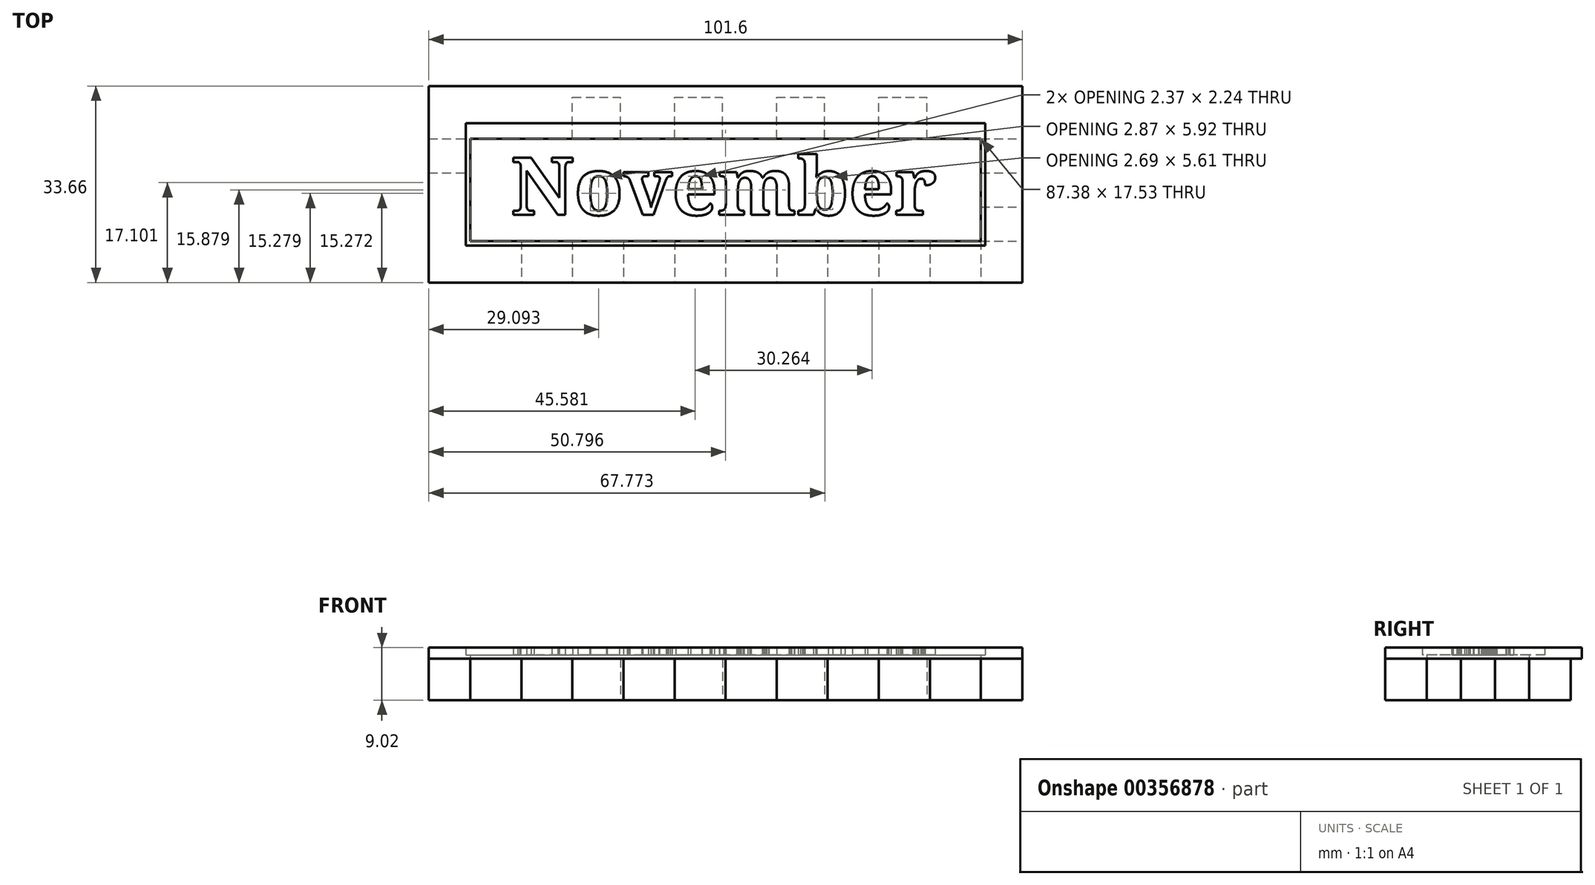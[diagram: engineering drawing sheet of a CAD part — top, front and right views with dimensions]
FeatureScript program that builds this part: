
annotation { "Feature Type Name" : "Feature", "Feature Type Description" : "" }
export const myFeature = defineFeature(function(context is Context, id is Id, definition is map)
    precondition{}
    {
        {
            var Q0;
            Q0=qCreatedBy(makeId("Top.planeOp"),FACE);
            var sketch = newSketch(context, id + "F0", { "sketchPlane" : qUnion([Q0])});
            skLineSegment(sketch, "E0.bottom", {"start": v(-52.12, 11.37) * mm, "end": v(49.48, 11.37) * mm});
            skLineSegment(sketch, "E0.top", {"start": v(-52.12, -20.38) * mm, "end": v(49.48, -20.38) * mm});
            skLineSegment(sketch, "E0.left", {"start": v(-52.12, 11.37) * mm, "end": v(-52.12, -20.38) * mm});
            skLineSegment(sketch, "E0.right", {"start": v(49.48, 11.37) * mm, "end": v(49.48, -20.38) * mm});
            skLineSegment(sketch, "E1.bottom", {"start": v(-52.12, 11.37) * mm, "end": v(-45.01, 11.37) * mm});
            skLineSegment(sketch, "E1.top", {"start": v(-52.12, 4.26) * mm, "end": v(-45.01, 4.26) * mm});
            skLineSegment(sketch, "E1.left", {"start": v(-52.12, 11.37) * mm, "end": v(-52.12, 4.26) * mm});
            skLineSegment(sketch, "E1.right", {"start": v(-45.01, 11.37) * mm, "end": v(-45.01, 4.26) * mm});
            skLineSegment(sketch, "E2.bottom", {"start": v(-45.01, 11.37) * mm, "end": v(-36.78, 11.37) * mm});
            skLineSegment(sketch, "E2.top", {"start": v(-45.01, 4.26) * mm, "end": v(-36.78, 4.26) * mm});
            skLineSegment(sketch, "E2.right", {"start": v(-36.78, 11.37) * mm, "end": v(-36.78, 4.26) * mm});
            skLineSegment(sketch, "E3.bottom", {"start": v(-36.78, 4.26) * mm, "end": v(-27.54, 4.26) * mm});
            skLineSegment(sketch, "E3.top", {"start": v(-36.78, 11.37) * mm, "end": v(-27.54, 11.37) * mm});
            skLineSegment(sketch, "E3.left", {"start": v(-36.78, 4.26) * mm, "end": v(-36.78, 11.37) * mm});
            skLineSegment(sketch, "E3.right", {"start": v(-27.54, 4.26) * mm, "end": v(-27.54, 11.37) * mm});
            skLineSegment(sketch, "E4.bottom", {"start": v(-27.54, 4.26) * mm, "end": v(-19.3, 4.26) * mm});
            skLineSegment(sketch, "E4.top", {"start": v(-27.54, 11.37) * mm, "end": v(-19.3, 11.37) * mm});
            skLineSegment(sketch, "E4.right", {"start": v(-19.3, 4.26) * mm, "end": v(-19.3, 11.37) * mm});
            skLineSegment(sketch, "E5.bottom", {"start": v(-19.3, 4.26) * mm, "end": v(-10.06, 4.26) * mm});
            skLineSegment(sketch, "E5.top", {"start": v(-19.3, 11.37) * mm, "end": v(-10.06, 11.37) * mm});
            skLineSegment(sketch, "E5.right", {"start": v(-10.06, 4.26) * mm, "end": v(-10.06, 11.37) * mm});
            skLineSegment(sketch, "E6.bottom", {"start": v(-10.06, 4.26) * mm, "end": v(-10.06, 4.26) * mm});
            skLineSegment(sketch, "E6.top", {"start": v(-10.06, 11.37) * mm, "end": v(-10.06, 11.37) * mm});
            skLineSegment(sketch, "E7.bottom", {"start": v(-10.06, 4.26) * mm, "end": v(-1.83, 4.26) * mm});
            skLineSegment(sketch, "E7.top", {"start": v(-10.06, 11.37) * mm, "end": v(-1.83, 11.37) * mm});
            skLineSegment(sketch, "E7.right", {"start": v(-1.83, 4.26) * mm, "end": v(-1.83, 11.37) * mm});
            skLineSegment(sketch, "E8.bottom", {"start": v(-1.83, 4.26) * mm, "end": v(7.41, 4.26) * mm});
            skLineSegment(sketch, "E8.top", {"start": v(-1.83, 11.37) * mm, "end": v(7.41, 11.37) * mm});
            skLineSegment(sketch, "E8.right", {"start": v(7.41, 4.26) * mm, "end": v(7.41, 11.37) * mm});
            skLineSegment(sketch, "E9.bottom", {"start": v(7.41, 4.26) * mm, "end": v(15.64, 4.26) * mm});
            skLineSegment(sketch, "E9.top", {"start": v(7.41, 11.37) * mm, "end": v(15.64, 11.37) * mm});
            skLineSegment(sketch, "E9.right", {"start": v(15.64, 4.26) * mm, "end": v(15.64, 11.37) * mm});
            skLineSegment(sketch, "E10.bottom", {"start": v(15.64, 4.26) * mm, "end": v(24.89, 4.26) * mm});
            skLineSegment(sketch, "E10.top", {"start": v(15.64, 11.37) * mm, "end": v(24.89, 11.37) * mm});
            skLineSegment(sketch, "E10.right", {"start": v(24.89, 4.26) * mm, "end": v(24.89, 11.37) * mm});
            skLineSegment(sketch, "E11.bottom", {"start": v(24.89, 4.26) * mm, "end": v(24.89, 4.26) * mm});
            skLineSegment(sketch, "E11.top", {"start": v(24.89, 11.37) * mm, "end": v(24.89, 11.37) * mm});
            skLineSegment(sketch, "E12.bottom", {"start": v(24.89, 4.26) * mm, "end": v(33.12, 4.26) * mm});
            skLineSegment(sketch, "E12.top", {"start": v(24.89, 11.37) * mm, "end": v(33.12, 11.37) * mm});
            skLineSegment(sketch, "E12.right", {"start": v(33.12, 4.26) * mm, "end": v(33.12, 11.37) * mm});
            skLineSegment(sketch, "E13.bottom", {"start": v(33.12, 4.26) * mm, "end": v(42.36, 4.26) * mm});
            skLineSegment(sketch, "E13.top", {"start": v(33.12, 11.37) * mm, "end": v(42.36, 11.37) * mm});
            skLineSegment(sketch, "E13.right", {"start": v(42.36, 4.26) * mm, "end": v(42.36, 11.37) * mm});
            skLineSegment(sketch, "E14.bottom", {"start": v(42.36, 4.26) * mm, "end": v(49.48, 4.26) * mm});
            skLineSegment(sketch, "E14.top", {"start": v(42.36, 11.37) * mm, "end": v(49.48, 11.37) * mm});
            skLineSegment(sketch, "E14.right", {"start": v(49.48, 4.26) * mm, "end": v(49.48, 11.37) * mm});
            skLineSegment(sketch, "E15.bottom", {"start": v(-52.12, -20.38) * mm, "end": v(-45.01, -20.38) * mm});
            skLineSegment(sketch, "E15.top", {"start": v(-52.12, -13.26) * mm, "end": v(-45.01, -13.26) * mm});
            skLineSegment(sketch, "E15.left", {"start": v(-52.12, -20.38) * mm, "end": v(-52.12, -13.26) * mm});
            skLineSegment(sketch, "E15.right", {"start": v(-45.01, -20.38) * mm, "end": v(-45.01, -13.26) * mm});
            skLineSegment(sketch, "E16.bottom", {"start": v(-45.01, -13.26) * mm, "end": v(-45.01, -13.26) * mm});
            skLineSegment(sketch, "E16.top", {"start": v(-45.01, -20.38) * mm, "end": v(-45.01, -20.38) * mm});
            skLineSegment(sketch, "E16.left", {"start": v(-45.01, -13.26) * mm, "end": v(-45.01, -20.38) * mm});
            skLineSegment(sketch, "E16.right", {"start": v(-45.01, -13.26) * mm, "end": v(-45.01, -20.38) * mm});
            skLineSegment(sketch, "E17.bottom", {"start": v(-45.01, -13.26) * mm, "end": v(-36.27, -13.26) * mm});
            skLineSegment(sketch, "E17.top", {"start": v(-45.01, -20.38) * mm, "end": v(-36.27, -20.38) * mm});
            skLineSegment(sketch, "E17.right", {"start": v(-36.27, -13.26) * mm, "end": v(-36.27, -20.38) * mm});
            skLineSegment(sketch, "E18.bottom", {"start": v(-36.27, -13.26) * mm, "end": v(-36.27, -13.26) * mm});
            skLineSegment(sketch, "E18.top", {"start": v(-36.27, -20.38) * mm, "end": v(-36.27, -20.38) * mm});
            skLineSegment(sketch, "E19.bottom", {"start": v(-36.27, -13.26) * mm, "end": v(-27.54, -13.26) * mm});
            skLineSegment(sketch, "E19.top", {"start": v(-36.27, -20.38) * mm, "end": v(-27.54, -20.38) * mm});
            skLineSegment(sketch, "E19.right", {"start": v(-27.54, -13.26) * mm, "end": v(-27.54, -20.38) * mm});
            skLineSegment(sketch, "E20.bottom", {"start": v(-27.54, -13.26) * mm, "end": v(-18.8, -13.26) * mm});
            skLineSegment(sketch, "E20.top", {"start": v(-27.54, -20.38) * mm, "end": v(-18.8, -20.38) * mm});
            skLineSegment(sketch, "E20.right", {"start": v(-18.8, -13.26) * mm, "end": v(-18.8, -20.38) * mm});
            skLineSegment(sketch, "E21.bottom", {"start": v(-18.8, -13.26) * mm, "end": v(-10.06, -13.26) * mm});
            skLineSegment(sketch, "E21.top", {"start": v(-18.8, -20.38) * mm, "end": v(-10.06, -20.38) * mm});
            skLineSegment(sketch, "E21.right", {"start": v(-10.06, -13.26) * mm, "end": v(-10.06, -20.38) * mm});
            skLineSegment(sketch, "E22.bottom", {"start": v(-10.06, -13.26) * mm, "end": v(-1.32, -13.26) * mm});
            skLineSegment(sketch, "E22.top", {"start": v(-10.06, -20.38) * mm, "end": v(-1.32, -20.38) * mm});
            skLineSegment(sketch, "E22.right", {"start": v(-1.32, -13.26) * mm, "end": v(-1.32, -20.38) * mm});
            skLineSegment(sketch, "E23.bottom", {"start": v(-1.32, -13.26) * mm, "end": v(7.41, -13.26) * mm});
            skLineSegment(sketch, "E23.top", {"start": v(-1.32, -20.38) * mm, "end": v(7.41, -20.38) * mm});
            skLineSegment(sketch, "E23.right", {"start": v(7.41, -13.26) * mm, "end": v(7.41, -20.38) * mm});
            skLineSegment(sketch, "E24.bottom", {"start": v(7.41, -13.26) * mm, "end": v(16.15, -13.26) * mm});
            skLineSegment(sketch, "E24.top", {"start": v(7.41, -20.38) * mm, "end": v(16.15, -20.38) * mm});
            skLineSegment(sketch, "E24.right", {"start": v(16.15, -13.26) * mm, "end": v(16.15, -20.38) * mm});
            skLineSegment(sketch, "E25.bottom", {"start": v(16.15, -13.26) * mm, "end": v(24.89, -13.26) * mm});
            skLineSegment(sketch, "E25.top", {"start": v(16.15, -20.38) * mm, "end": v(24.89, -20.38) * mm});
            skLineSegment(sketch, "E25.right", {"start": v(24.89, -13.26) * mm, "end": v(24.89, -20.38) * mm});
            skLineSegment(sketch, "E26.bottom", {"start": v(24.89, -13.26) * mm, "end": v(33.63, -13.26) * mm});
            skLineSegment(sketch, "E26.top", {"start": v(24.89, -20.38) * mm, "end": v(33.63, -20.38) * mm});
            skLineSegment(sketch, "E26.right", {"start": v(33.63, -13.26) * mm, "end": v(33.63, -20.38) * mm});
            skLineSegment(sketch, "E27.bottom", {"start": v(33.63, -13.26) * mm, "end": v(42.36, -13.26) * mm});
            skLineSegment(sketch, "E27.top", {"start": v(33.63, -20.38) * mm, "end": v(42.36, -20.38) * mm});
            skLineSegment(sketch, "E27.right", {"start": v(42.36, -13.26) * mm, "end": v(42.36, -20.38) * mm});
            skLineSegment(sketch, "E28.bottom", {"start": v(42.36, -13.26) * mm, "end": v(49.48, -13.26) * mm});
            skLineSegment(sketch, "E28.top", {"start": v(42.36, -20.38) * mm, "end": v(49.48, -20.38) * mm});
            skLineSegment(sketch, "E28.right", {"start": v(49.48, -13.26) * mm, "end": v(49.48, -20.38) * mm});
            skLineSegment(sketch, "E29.top", {"start": v(-52.12, -1.58) * mm, "end": v(-45.01, -1.58) * mm});
            skLineSegment(sketch, "E29.left", {"start": v(-52.12, 4.26) * mm, "end": v(-52.12, -1.58) * mm});
            skLineSegment(sketch, "E29.right", {"start": v(-45.01, 4.26) * mm, "end": v(-45.01, -1.58) * mm});
            skLineSegment(sketch, "E30.top", {"start": v(-52.12, -7.42) * mm, "end": v(-45.01, -7.42) * mm});
            skLineSegment(sketch, "E30.left", {"start": v(-52.12, -1.58) * mm, "end": v(-52.12, -7.42) * mm});
            skLineSegment(sketch, "E30.right", {"start": v(-45.01, -1.58) * mm, "end": v(-45.01, -7.42) * mm});
            skLineSegment(sketch, "E31.bottom", {"start": v(-45.01, -7.42) * mm, "end": v(-52.12, -7.42) * mm});
            skLineSegment(sketch, "E31.top", {"start": v(-45.01, -13.26) * mm, "end": v(-52.12, -13.26) * mm});
            skLineSegment(sketch, "E31.left", {"start": v(-45.01, -7.42) * mm, "end": v(-45.01, -13.26) * mm});
            skLineSegment(sketch, "E31.right", {"start": v(-52.12, -7.42) * mm, "end": v(-52.12, -13.26) * mm});
            skLineSegment(sketch, "E32.top", {"start": v(42.36, -1.58) * mm, "end": v(49.48, -1.58) * mm});
            skLineSegment(sketch, "E32.left", {"start": v(42.36, 4.26) * mm, "end": v(42.36, -1.58) * mm});
            skLineSegment(sketch, "E32.right", {"start": v(49.48, 4.26) * mm, "end": v(49.48, -1.58) * mm});
            skLineSegment(sketch, "E33.top", {"start": v(42.36, -7.42) * mm, "end": v(49.48, -7.42) * mm});
            skLineSegment(sketch, "E33.left", {"start": v(42.36, -1.58) * mm, "end": v(42.36, -7.42) * mm});
            skLineSegment(sketch, "E33.right", {"start": v(49.48, -1.58) * mm, "end": v(49.48, -7.42) * mm});
            skLineSegment(sketch, "E34.left", {"start": v(42.36, -7.42) * mm, "end": v(42.36, -13.26) * mm});
            skLineSegment(sketch, "E34.right", {"start": v(49.48, -7.42) * mm, "end": v(49.48, -13.26) * mm});
            skSolve(sketch);
        }
        {
            var Q0;
            Q0=makeQuery(id+"F0.imprint","IMPRINT",FACE,{"disambiguationData":[TD([[makeQuery(id+"F0.imprint","IMPRINT",EDGE,{"derivedFrom":sQuery(id+"F0.wireOp",EDGE,"E2.top")}),-1.0]])]});
            var Q1;
            Q1=makeQuery(id+"F0.imprint","IMPRINT",FACE,{"disambiguationData":[TD([[makeQuery(id+"F0.imprint","IMPRINT",EDGE,{"derivedFrom":sQuery(id+"F0.wireOp",EDGE,"E2.bottom")}),-1.0]])]});
            var Q2;
            Q2=makeQuery(id+"F0.imprint","IMPRINT",FACE,{"disambiguationData":[TD([[makeQuery(id+"F0.imprint","IMPRINT",EDGE,{"derivedFrom":sQuery(id+"F0.wireOp",EDGE,"E4.bottom")}),1.0]])]});
            var Q3;
            Q3=makeQuery(id+"F0.imprint","IMPRINT",FACE,{"disambiguationData":[TD([[makeQuery(id+"F0.imprint","IMPRINT",EDGE,{"derivedFrom":sQuery(id+"F0.wireOp",EDGE,"E7.bottom")}),1.0]])]});
            var Q4;
            Q4=makeQuery(id+"F0.imprint","IMPRINT",FACE,{"disambiguationData":[TD([[makeQuery(id+"F0.imprint","IMPRINT",EDGE,{"derivedFrom":sQuery(id+"F0.wireOp",EDGE,"E9.bottom")}),1.0]])]});
            var Q5;
            Q5=makeQuery(id+"F0.imprint","IMPRINT",FACE,{"disambiguationData":[TD([[makeQuery(id+"F0.imprint","IMPRINT",EDGE,{"derivedFrom":sQuery(id+"F0.wireOp",EDGE,"E12.bottom")}),1.0]])]});
            var Q6;
            Q6=makeQuery(id+"F0.imprint","IMPRINT",FACE,{"disambiguationData":[TD([[makeQuery(id+"F0.imprint","IMPRINT",EDGE,{"derivedFrom":sQuery(id+"F0.wireOp",EDGE,"E14.bottom")}),-1.0]])]});
            var Q7;
            Q7=makeQuery(id+"F0.imprint","IMPRINT",FACE,{"disambiguationData":[TD([[makeQuery(id+"F0.imprint","IMPRINT",EDGE,{"derivedFrom":sQuery(id+"F0.wireOp",EDGE,"E33.top")}),-1.0]])]});
            var Q8;
            Q8=makeQuery(id+"F0.imprint","IMPRINT",FACE,{"disambiguationData":[TD([[makeQuery(id+"F0.imprint","IMPRINT",EDGE,{"derivedFrom":sQuery(id+"F0.wireOp",EDGE,"E27.bottom")}),-1.0]])]});
            var Q9;
            Q9=makeQuery(id+"F0.imprint","IMPRINT",FACE,{"disambiguationData":[TD([[makeQuery(id+"F0.imprint","IMPRINT",EDGE,{"derivedFrom":sQuery(id+"F0.wireOp",EDGE,"E25.bottom")}),-1.0]])]});
            var Q10;
            Q10=makeQuery(id+"F0.imprint","IMPRINT",FACE,{"disambiguationData":[TD([[makeQuery(id+"F0.imprint","IMPRINT",EDGE,{"derivedFrom":sQuery(id+"F0.wireOp",EDGE,"E23.bottom")}),-1.0]])]});
            var Q11;
            Q11=makeQuery(id+"F0.imprint","IMPRINT",FACE,{"disambiguationData":[TD([[makeQuery(id+"F0.imprint","IMPRINT",EDGE,{"derivedFrom":sQuery(id+"F0.wireOp",EDGE,"E21.bottom")}),-1.0]])]});
            var Q12;
            Q12=makeQuery(id+"F0.imprint","IMPRINT",FACE,{"disambiguationData":[TD([[makeQuery(id+"F0.imprint","IMPRINT",EDGE,{"derivedFrom":sQuery(id+"F0.wireOp",EDGE,"E19.bottom")}),-1.0]])]});
            var Q13;
            Q13=makeQuery(id+"F0.imprint","IMPRINT",FACE,{"disambiguationData":[TD([[makeQuery(id+"F0.imprint","IMPRINT",EDGE,{"derivedFrom":sQuery(id+"F0.wireOp",EDGE,"E31.bottom")}),1.0]])]});
            var Q14;
            Q14=makeQuery(id+"F0.imprint","IMPRINT",FACE,{"disambiguationData":[TD([[makeQuery(id+"F0.imprint","IMPRINT",EDGE,{"derivedFrom":sQuery(id+"F0.wireOp",EDGE,"E1.top")}),-1.0]])]});
            extrude(context, id + "F1", {"entities" : qUnion([Q0, Q1, Q2, Q3, Q4, Q5, Q6, Q7, Q8, Q9, Q10, Q11, Q12, Q13, Q14]), "depth" : 7.11 * mm});
        }
        {
            var Q0;
            Q0=makeQuery(id+"F1.opExtrude","CAP_FACE",FACE,{"disambiguationData":[OSD([sQuery(id+"F0.wireOp",EDGE,"E2.bottom"),sQuery(id+"F0.wireOp",EDGE,"E1.right"),sQuery(id+"F0.wireOp",EDGE,"E3.bottom"),sQuery(id+"F0.wireOp",EDGE,"E3.left"),sQuery(id+"F0.wireOp",EDGE,"E4.top"),sQuery(id+"F0.wireOp",EDGE,"E3.right"),sQuery(id+"F0.wireOp",EDGE,"E5.bottom"),sQuery(id+"F0.wireOp",EDGE,"E4.right"),sQuery(id+"F0.wireOp",EDGE,"E6.top"),sQuery(id+"F0.wireOp",EDGE,"E5.right"),sQuery(id+"F0.wireOp",EDGE,"E7.bottom"),sQuery(id+"F0.wireOp",EDGE,"E5.right"),sQuery(id+"F0.wireOp",EDGE,"E8.top"),sQuery(id+"F0.wireOp",EDGE,"E7.right"),sQuery(id+"F0.wireOp",EDGE,"E9.bottom"),sQuery(id+"F0.wireOp",EDGE,"E8.right"),sQuery(id+"F0.wireOp",EDGE,"E10.top"),sQuery(id+"F0.wireOp",EDGE,"E9.right"),sQuery(id+"F0.wireOp",EDGE,"E11.bottom"),sQuery(id+"F0.wireOp",EDGE,"E10.right"),sQuery(id+"F0.wireOp",EDGE,"E12.top"),sQuery(id+"F0.wireOp",EDGE,"E10.right"),sQuery(id+"F0.wireOp",EDGE,"E13.bottom"),sQuery(id+"F0.wireOp",EDGE,"E12.right"),sQuery(id+"F0.wireOp",EDGE,"E16.bottom"),sQuery(id+"F0.wireOp",EDGE,"E17.top"),sQuery(id+"F0.wireOp",EDGE,"E16.left"),sQuery(id+"F0.wireOp",EDGE,"E18.bottom"),sQuery(id+"F0.wireOp",EDGE,"E17.right"),sQuery(id+"F0.wireOp",EDGE,"E19.top"),sQuery(id+"F0.wireOp",EDGE,"E17.right"),sQuery(id+"F0.wireOp",EDGE,"E20.bottom"),sQuery(id+"F0.wireOp",EDGE,"E19.right"),sQuery(id+"F0.wireOp",EDGE,"E21.top"),sQuery(id+"F0.wireOp",EDGE,"E20.right"),sQuery(id+"F0.wireOp",EDGE,"E22.bottom"),sQuery(id+"F0.wireOp",EDGE,"E21.right"),sQuery(id+"F0.wireOp",EDGE,"E23.top"),sQuery(id+"F0.wireOp",EDGE,"E22.right"),sQuery(id+"F0.wireOp",EDGE,"E24.bottom"),sQuery(id+"F0.wireOp",EDGE,"E23.right"),sQuery(id+"F0.wireOp",EDGE,"E25.top"),sQuery(id+"F0.wireOp",EDGE,"E24.right"),sQuery(id+"F0.wireOp",EDGE,"E26.bottom"),sQuery(id+"F0.wireOp",EDGE,"E25.right"),sQuery(id+"F0.wireOp",EDGE,"E27.top"),sQuery(id+"F0.wireOp",EDGE,"E26.right"),sQuery(id+"F0.wireOp",EDGE,"E27.right"),sQuery(id+"F0.wireOp",EDGE,"E1.top"),sQuery(id+"F0.wireOp",EDGE,"E29.left"),sQuery(id+"F0.wireOp",EDGE,"E29.top"),sQuery(id+"F0.wireOp",EDGE,"E30.right"),sQuery(id+"F0.wireOp",EDGE,"E31.bottom"),sQuery(id+"F0.wireOp",EDGE,"E31.top"),sQuery(id+"F0.wireOp",EDGE,"E31.right"),sQuery(id+"F0.wireOp",EDGE,"E14.bottom"),sQuery(id+"F0.wireOp",EDGE,"E32.right"),sQuery(id+"F0.wireOp",EDGE,"E32.top"),sQuery(id+"F0.wireOp",EDGE,"E33.left"),sQuery(id+"F0.wireOp",EDGE,"E33.top"),sQuery(id+"F0.wireOp",EDGE,"E28.bottom"),sQuery(id+"F0.wireOp",EDGE,"E34.right")])],"isStart":false});
            var sketch = newSketch(context, id + "F2", { "sketchPlane" : qUnion([Q0])});
            skLineSegment(sketch, "E35.bottom", {"start": v(-52.12, -20.38) * mm, "end": v(-45.01, -20.38) * mm});
            skLineSegment(sketch, "E35.top", {"start": v(-52.12, 13.28) * mm, "end": v(-45.01, 13.28) * mm});
            skLineSegment(sketch, "E35.left", {"start": v(-52.12, -20.38) * mm, "end": v(-52.12, 13.28) * mm});
            skLineSegment(sketch, "E35.right", {"start": v(-45.01, -20.38) * mm, "end": v(-45.01, 13.28) * mm});
            skLineSegment(sketch, "E36.bottom", {"start": v(-52.12, -20.38) * mm, "end": v(49.48, -20.38) * mm});
            skLineSegment(sketch, "E36.top", {"start": v(-52.12, -13.26) * mm, "end": v(49.48, -13.26) * mm});
            skLineSegment(sketch, "E36.left", {"start": v(-52.12, -20.38) * mm, "end": v(-52.12, -13.26) * mm});
            skLineSegment(sketch, "E36.right", {"start": v(49.48, -20.38) * mm, "end": v(49.48, -13.26) * mm});
            skPoint(sketch, "E37.oppositeSnap0", {"position": v(42.36, -4.5) * mm});
            skLineSegment(sketch, "E37.bottom", {"start": v(49.48, -20.38) * mm, "end": v(42.36, -20.38) * mm});
            skLineSegment(sketch, "E37.top", {"start": v(49.48, 13.28) * mm, "end": v(42.36, 13.28) * mm});
            skLineSegment(sketch, "E37.left", {"start": v(49.48, -20.38) * mm, "end": v(49.48, 13.28) * mm});
            skLineSegment(sketch, "E37.right", {"start": v(42.36, -20.38) * mm, "end": v(42.36, 13.28) * mm});
            skLineSegment(sketch, "E38.bottom", {"start": v(-52.12, 13.28) * mm, "end": v(49.48, 13.28) * mm});
            skLineSegment(sketch, "E38.top", {"start": v(-52.12, 4.26) * mm, "end": v(49.48, 4.26) * mm});
            skLineSegment(sketch, "E38.left", {"start": v(-52.12, 13.28) * mm, "end": v(-52.12, 4.26) * mm});
            skLineSegment(sketch, "E38.right", {"start": v(49.48, 13.28) * mm, "end": v(49.48, 4.26) * mm});
            skSolve(sketch);
        }
        {
            var Q0;
            Q0=qSketchRegion(id+"F2",true);
            var Q1;
            {var subQ5=sQuery(id+"F2.wireOp",EDGE,"E36.top");var subQ10=sQuery(id+"F2.wireOp",EDGE,"E35.right");var subQ12=makeQuery(id+"F2.imprint","INTERSECT",VERTEX,{"derivedFrom":[makeQuery(id+"F1.opExtrude","CAP_EDGE",EDGE,{"disambiguationData":[OSD([sQuery(id+"F0.wireOp",EDGE,"E31.bottom")])],"isStart":false}),subQ10]});var subQ24=makeQuery(id+"F2.imprint","INTERSECT",VERTEX,{"derivedFrom":[subQ10,subQ5]});Q1=makeQuery(id+"F2.imprint","IMPRINT",FACE,{"disambiguationData":[TD([[makeQuery(id+"F2.imprint","IMPRINT",EDGE,{"disambiguationData":[TD([[subQ12,1.0],[subQ24,-1.0]])],"derivedFrom":subQ10}),-1.0]])]});}
            extrude(context, id + "F3", {"entities" : qUnion([Q0, Q1]), "depth" : 0.64 * mm});
        }
        {
            var Q0;
            Q0=makeQuery(id+"F3.opExtrude","CAP_FACE",FACE,{"disambiguationData":[OSD([sQuery(id+"F2.wireOp",EDGE,"E35.left"),sQuery(id+"F2.wireOp",EDGE,"E36.bottom"),sQuery(id+"F2.wireOp",EDGE,"E36.left"),sQuery(id+"F2.wireOp",EDGE,"E37.bottom"),sQuery(id+"F2.wireOp",EDGE,"E37.left"),sQuery(id+"F2.wireOp",EDGE,"E38.bottom"),sQuery(id+"F2.wireOp",EDGE,"E38.left"),sQuery(id+"F2.wireOp",EDGE,"E38.right")])],"isStart":false});
            var sketch = newSketch(context, id + "F4", { "sketchPlane" : qUnion([Q0])});
            skLineSegment(sketch, "E39.bottom", {"start": v(-52.12, 13.28) * mm, "end": v(49.48, 13.28) * mm});
            skLineSegment(sketch, "E39.top", {"start": v(-52.12, 6.93) * mm, "end": v(49.48, 6.93) * mm});
            skLineSegment(sketch, "E39.left", {"start": v(-52.12, 13.28) * mm, "end": v(-52.12, 6.93) * mm});
            skLineSegment(sketch, "E39.right", {"start": v(49.48, 13.28) * mm, "end": v(49.48, 6.93) * mm});
            skLineSegment(sketch, "E40.bottom", {"start": v(-52.12, 13.28) * mm, "end": v(-45.77, 13.28) * mm});
            skLineSegment(sketch, "E40.top", {"start": v(-52.12, -20.38) * mm, "end": v(-45.77, -20.38) * mm});
            skLineSegment(sketch, "E40.left", {"start": v(-52.12, 13.28) * mm, "end": v(-52.12, -20.38) * mm});
            skLineSegment(sketch, "E40.right", {"start": v(-45.77, 13.28) * mm, "end": v(-45.77, -20.38) * mm});
            skLineSegment(sketch, "E41.bottom", {"start": v(-52.12, -14.03) * mm, "end": v(49.48, -14.03) * mm});
            skLineSegment(sketch, "E41.top", {"start": v(-52.12, -20.38) * mm, "end": v(49.48, -20.38) * mm});
            skLineSegment(sketch, "E41.left", {"start": v(-52.12, -14.03) * mm, "end": v(-52.12, -20.38) * mm});
            skLineSegment(sketch, "E41.right", {"start": v(49.48, -14.03) * mm, "end": v(49.48, -20.38) * mm});
            skLineSegment(sketch, "E42.bottom", {"start": v(49.48, -20.38) * mm, "end": v(43.13, -20.38) * mm});
            skLineSegment(sketch, "E42.top", {"start": v(49.48, 13.28) * mm, "end": v(43.13, 13.28) * mm});
            skLineSegment(sketch, "E42.left", {"start": v(49.48, -20.38) * mm, "end": v(49.48, 13.28) * mm});
            skLineSegment(sketch, "E42.right", {"start": v(43.13, -20.38) * mm, "end": v(43.13, 13.28) * mm});
            skSolve(sketch);
        }
        {
            var Q0;
            Q0=qSketchRegion(id+"F4",true);
            extrude(context, id + "F5", {"entities" : qUnion([Q0]), "operationType" : NewBodyOperationType.ADD, "depth" : 1.27 * mm});
        }
        {
            var Q0;
            Q0=makeQuery(id+"F3.opExtrude","CAP_FACE",FACE,{"disambiguationData":[OSD([sQuery(id+"F2.wireOp",EDGE,"E35.left"),sQuery(id+"F2.wireOp",EDGE,"E36.bottom"),sQuery(id+"F2.wireOp",EDGE,"E36.left"),sQuery(id+"F2.wireOp",EDGE,"E37.bottom"),sQuery(id+"F2.wireOp",EDGE,"E37.left"),sQuery(id+"F2.wireOp",EDGE,"E38.bottom"),sQuery(id+"F2.wireOp",EDGE,"E38.left"),sQuery(id+"F2.wireOp",EDGE,"E38.right")])],"isStart":false});
            var sketch = newSketch(context, id + "F6", { "sketchPlane" : qUnion([Q0])});
            skText(sketch, "E43", { "text": "November", "fontName": "NotoSerif-Bold.ttf"});
            const initialGuessF6  = {"E43": [-0.03805, -0.0088, 1, 0, 0.00988]};
            skSetInitialGuess(sketch, initialGuessF6);
            skSolve(sketch);
        }
        {
            var Q0;
            Q0 = qSketchRegion(id + "F6", true);
            extrude(context, id + "F7", {"entities" : qUnion([Q0]), "operationType" : NewBodyOperationType.ADD, "depth" : 1.27 * mm});
        }
    });
